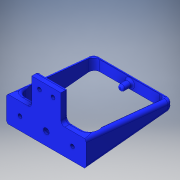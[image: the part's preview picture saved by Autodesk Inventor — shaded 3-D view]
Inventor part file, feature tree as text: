
AUTODESK INVENTOR PART (.ipt)
format: ipt  version: 2016 (Build 200138000, 138)  size: 363,008 bytes
history: native  units: in
note: dims shown in document units (in); Inventor stores cm internally (conversion verified against a paired STEP export)
features: sketch x11, other x3
ambient origin geometry x8: Origin, YZ Plane, XZ Plane, XY Plane, X Axis, Y Axis, Z Axis, Center Point
bodies: Solid1 (feature_tree)
feature tree (14):
  other  "Knee_hip_joint_right_side.ipt"
  other  "Solid1::Knee_hip_joint_right_side.ipt"
  other  "TaggingFeature1"
  sketch  "Sketch1"  dims[d0=0.3937in]
  sketch  "Sketch16"
  sketch  "Sketch17"
  sketch  "Sketch19"
  sketch  "Sketch20"
  sketch  "Sketch22"
  sketch  "Sketch24"
  sketch  "Sketch25"
  sketch  "Sketch30"
  sketch  "Sketch31"
  sketch  "Sketch32"
